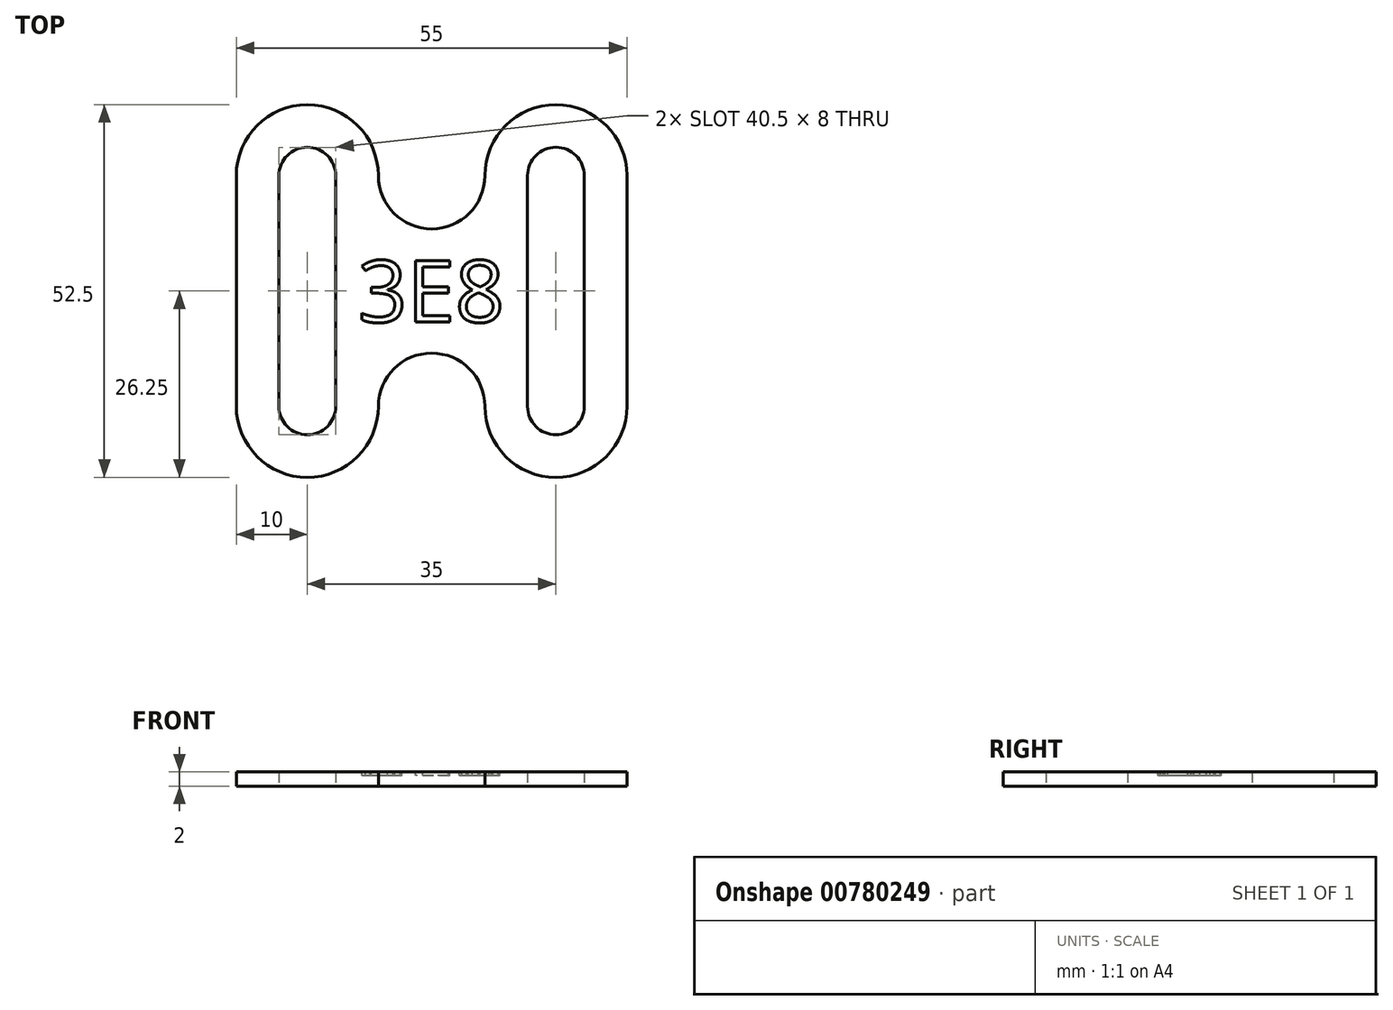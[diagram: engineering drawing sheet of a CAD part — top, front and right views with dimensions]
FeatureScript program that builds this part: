
annotation { "Feature Type Name" : "Feature", "Feature Type Description" : "" }
export const myFeature = defineFeature(function(context is Context, id is Id, definition is map)
    precondition{}
    {
        {
            var Q0;
            Q0=qCreatedBy(makeId("Top.planeOp"),FACE);
            var sketch = newSketch(context, id + "F0", { "sketchPlane" : qUnion([Q0])});
            skLineSegment(sketch, "E0", {"start": v(-17.5, 0) * mm, "end": v(17.5, 0) * mm, "construction": true});
            skLineSegment(sketch, "E1", {"start": v(0, 8.75) * mm, "end": v(0, -8.75) * mm, "construction": true});
            skLineSegment(sketch, "E2", {"start": v(-17.5, 16.25) * mm, "end": v(-17.5, -16.25) * mm, "construction": true});
            skArc(sketch, "E3", {"start": v(-7.5, 16.25) * mm, "mid": v(-17.5, 26.25) * mm, "end": v(-27.5, 16.25) * mm});
            skLineSegment(sketch, "E4", {"start": v(-27.5, 16.25) * mm, "end": v(-27.5, -16.25) * mm});
            skArc(sketch, "E5.MirrorCS", {"start": v(-7.5, -16.25) * mm, "mid": v(-17.5, -26.25) * mm, "end": v(-27.5, -16.25) * mm});
            skArc(sketch, "E6", {"start": v(-7.5, 16.25) * mm, "mid": v(0, 8.75) * mm, "end": v(7.5, 16.25) * mm});
            skLineSegment(sketch, "E7", {"start": v(-7.5, 16.25) * mm, "end": v(7.5, 16.25) * mm, "construction": true});
            skLineSegment(sketch, "E8", {"start": v(-27.5, 16.25) * mm, "end": v(-7.5, 16.25) * mm, "construction": true});
            skArc(sketch, "E9.MirrorCS", {"start": v(-7.5, -16.25) * mm, "mid": v(0, -8.75) * mm, "end": v(7.5, -16.25) * mm});
            skArc(sketch, "E10.MirrorCS", {"start": v(7.5, 16.25) * mm, "mid": v(17.5, 26.25) * mm, "end": v(27.5, 16.25) * mm});
            skLineSegment(sketch, "E11.MirrorCS", {"start": v(27.5, 16.25) * mm, "end": v(27.5, -16.25) * mm});
            skArc(sketch, "E12.MirrorCS", {"start": v(7.5, -16.25) * mm, "mid": v(17.5, -26.25) * mm, "end": v(27.5, -16.25) * mm});
            skLineSegment(sketch, "E13", {"start": v(-7.5, 16.25) * mm, "end": v(-7.5, -16.25) * mm, "construction": true});
            skArc(sketch, "E14.0", {"start": v(-13.5, 16.25) * mm, "mid": v(-17.5, 20.25) * mm, "end": v(-21.5, 16.25) * mm});
            skLineSegment(sketch, "E14.1", {"start": v(-13.5, 16.25) * mm, "end": v(-13.5, -16.25) * mm});
            skArc(sketch, "E14.2", {"start": v(-13.5, -16.25) * mm, "mid": v(-17.5, -20.25) * mm, "end": v(-21.5, -16.25) * mm});
            skLineSegment(sketch, "E14.3", {"start": v(-21.5, 16.25) * mm, "end": v(-21.5, -16.25) * mm});
            skLineSegment(sketch, "E15.MirrorCS", {"start": v(13.5, 16.25) * mm, "end": v(13.5, -16.25) * mm});
            skArc(sketch, "E16.MirrorCS", {"start": v(13.5, 16.25) * mm, "mid": v(17.5, 20.25) * mm, "end": v(21.5, 16.25) * mm});
            skLineSegment(sketch, "E17.MirrorCS", {"start": v(21.5, 16.25) * mm, "end": v(21.5, -16.25) * mm});
            skArc(sketch, "E18.MirrorCS", {"start": v(13.5, -16.25) * mm, "mid": v(17.5, -20.25) * mm, "end": v(21.5, -16.25) * mm});
            skSolve(sketch);
        }
        {
            var Q0;
            Q0 = qSketchRegion(id + "F0", true);
            extrude(context, id + "F1", {"entities" : qUnion([Q0]), "depth" : 2 * mm, "offsetDistance" : 25 * mm});
        }
        {
            var Q0;
            Q0=makeQuery(id+"F1.opExtrude","CAP_FACE",FACE,{"disambiguationData":[OSD([sQuery(id+"F0.wireOp",EDGE,"E3"),sQuery(id+"F0.wireOp",EDGE,"E4"),sQuery(id+"F0.wireOp",EDGE,"E5.MirrorCS"),sQuery(id+"F0.wireOp",EDGE,"E6"),sQuery(id+"F0.wireOp",EDGE,"E9.MirrorCS"),sQuery(id+"F0.wireOp",EDGE,"E10.MirrorCS"),sQuery(id+"F0.wireOp",EDGE,"E11.MirrorCS"),sQuery(id+"F0.wireOp",EDGE,"E12.MirrorCS"),sQuery(id+"F0.wireOp",EDGE,"E14.0"),sQuery(id+"F0.wireOp",EDGE,"E14.1"),sQuery(id+"F0.wireOp",EDGE,"E14.2"),sQuery(id+"F0.wireOp",EDGE,"E14.3"),sQuery(id+"F0.wireOp",EDGE,"E15.MirrorCS"),sQuery(id+"F0.wireOp",EDGE,"E16.MirrorCS"),sQuery(id+"F0.wireOp",EDGE,"E17.MirrorCS"),sQuery(id+"F0.wireOp",EDGE,"E18.MirrorCS")])],"isStart":false});
            var sketch = newSketch(context, id + "F2", { "sketchPlane" : qUnion([Q0])});
            skText(sketch, "E19", { "text": "3E8", "fontName": "OpenSans-Regular.ttf"});
            const initialGuessF2  = {"E19": [-0.0104, -0.00438, 1, 0, 0.00875]};
            skSetInitialGuess(sketch, initialGuessF2);
            skSolve(sketch);
        }
        {
            var Q0;
            Q0 = qSketchRegion(id + "F2", true);
            extrude(context, id + "F3", {"entities" : qUnion([Q0]), "operationType" : NewBodyOperationType.REMOVE, "oppositeDirection" : true, "depth" : .5 * mm, "offsetDistance" : 25 * mm});
        }
    });
